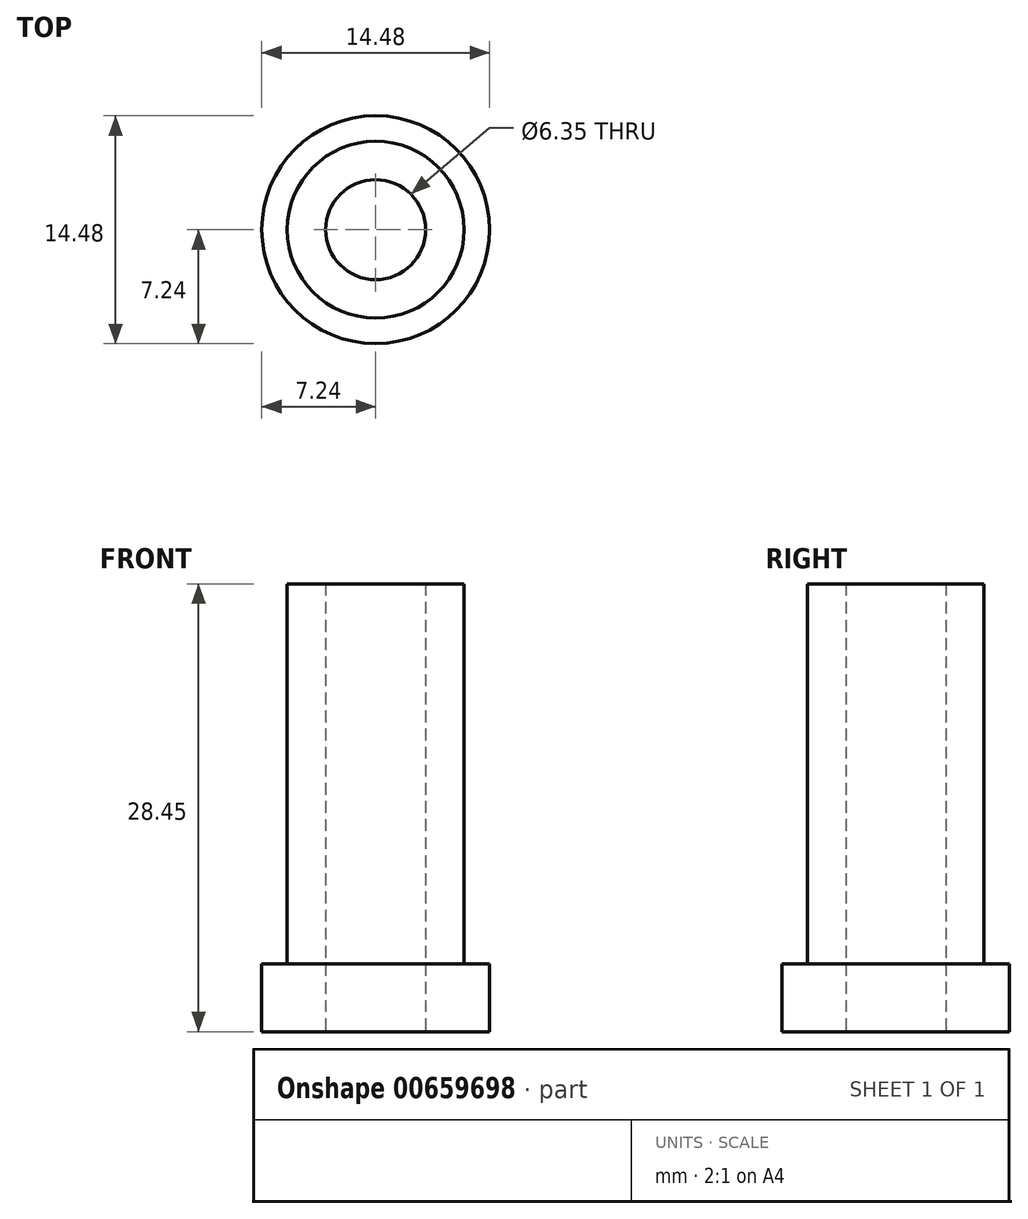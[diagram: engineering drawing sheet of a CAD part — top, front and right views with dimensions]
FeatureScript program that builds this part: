
annotation { "Feature Type Name" : "Feature", "Feature Type Description" : "" }
export const myFeature = defineFeature(function(context is Context, id is Id, definition is map)
    precondition{}
    {
        {
            var Q0;
            Q0=qCreatedBy(makeId("Top.planeOp"),FACE);
            var sketch = newSketch(context, id + "F0", { "sketchPlane" : qUnion([Q0])});
            skCircle(sketch, "E0", {"center": v(0, 0) * mm, "radius": 5.62 * mm});
            skSolve(sketch);
        }
        {
            var Q0;
            Q0 = qSketchRegion(id + "F0", true);
            extrude(context, id + "F1", {"entities" : qUnion([Q0]), "depth" : 28.45 * mm, "offsetDistance" : 25.4 * mm});
        }
        {
            var Q0;
            Q0=qCreatedBy(makeId("Top.planeOp"),FACE);
            var sketch = newSketch(context, id + "F2", { "sketchPlane" : qUnion([Q0])});
            skCircle(sketch, "E1", {"center": v(0, 0) * mm, "radius": 7.24 * mm});
            skSolve(sketch);
        }
        {
            var Q0;
            Q0 = qSketchRegion(id + "F2", true);
            extrude(context, id + "F3", {"entities" : qUnion([Q0]), "operationType" : NewBodyOperationType.ADD, "depth" : 4.32 * mm, "offsetDistance" : 25.4 * mm});
        }
        {
            var Q0;
            Q0=qCreatedBy(makeId("Top.planeOp"),FACE);
            var sketch = newSketch(context, id + "F4", { "sketchPlane" : qUnion([Q0])});
            skCircle(sketch, "E2", {"center": v(0, 0) * mm, "radius": 4.07 * mm});
            skSolve(sketch);
        }
        {
            var Q0;
            Q0=sQuery(id+"F4.wireOp",VERTEX,"E2.center");
            var Q1;
            Q1=makeQuery(id+"F1.opExtrude","SWEPT_BODY",BODY,{"disambiguationData":[OSD([sQuery(id+"F0.wireOp",EDGE,"E0")])]});
            hole(context, id + "F5", {"style" : HoleStyle.SIMPLE, "endStyle" : HoleEndStyle.THROUGH, "oppositeDirection" : true, "holeDiameter" : 6.35 * mm, "majorDiameter" : 6.35 * mm, "isTappedThrough" : true, "tappedDepth" : 12.7 * mm, "tapClearance" : 3, "locations" : qUnion([Q0]), "scope" : qUnion([Q1])});
        }
    });
